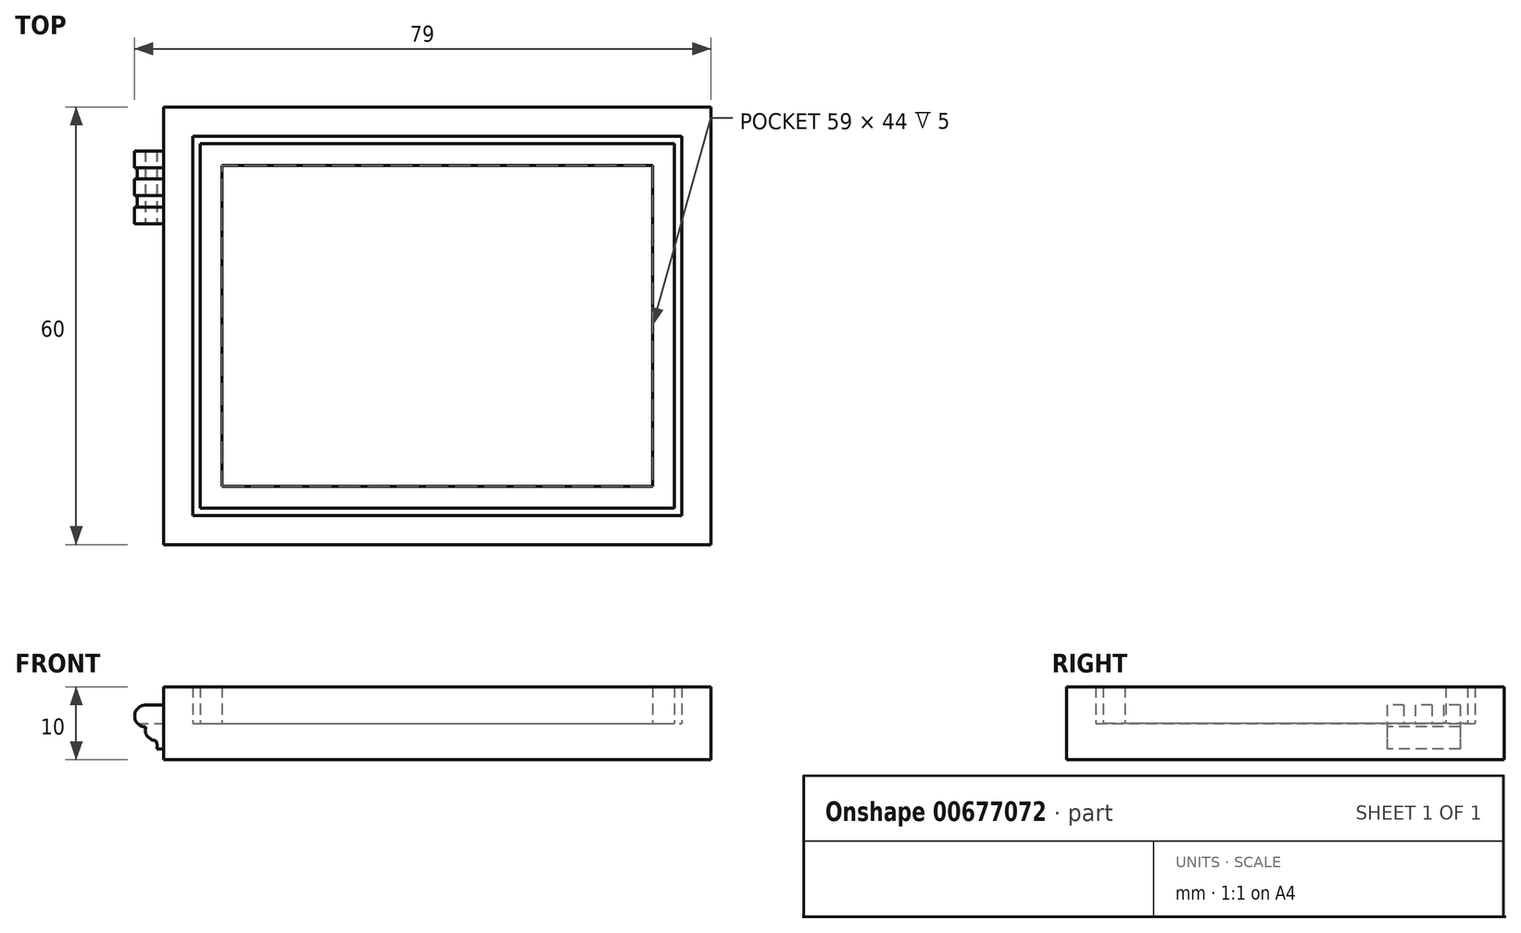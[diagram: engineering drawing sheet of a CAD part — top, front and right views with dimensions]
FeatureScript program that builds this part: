
annotation { "Feature Type Name" : "Feature", "Feature Type Description" : "" }
export const myFeature = defineFeature(function(context is Context, id is Id, definition is map)
    precondition{}
    {
        {
            var Q0;
            Q0=qCreatedBy(makeId("Top.planeOp"),FACE);
            var sketch = newSketch(context, id + "F0", { "sketchPlane" : qUnion([Q0])});
            skLineSegment(sketch, "E0.bottom", {"start": v(-37.5, 30) * mm, "end": v(37.5, 30) * mm});
            skLineSegment(sketch, "E0.top", {"start": v(-37.5, -30) * mm, "end": v(37.5, -30) * mm});
            skLineSegment(sketch, "E0.left", {"start": v(-37.5, 30) * mm, "end": v(-37.5, -30) * mm});
            skLineSegment(sketch, "E0.right", {"start": v(37.5, 30) * mm, "end": v(37.5, -30) * mm});
            skSolve(sketch);
        }
        {
            var Q0;
            Q0 = qSketchRegion(id + "F0", true);
            extrude(context, id + "F1", {"entities" : qUnion([Q0]), "depth" : 5 * mm, "offsetDistance" : 25 * mm});
        }
        {
            var Q0;
            Q0=makeQuery(id+"F1.opExtrude","CAP_FACE",FACE,{"disambiguationData":[OSD([sQuery(id+"F0.wireOp",EDGE,"E0.bottom"),sQuery(id+"F0.wireOp",EDGE,"E0.top"),sQuery(id+"F0.wireOp",EDGE,"E0.left"),sQuery(id+"F0.wireOp",EDGE,"E0.right")])],"isStart":false});
            var sketch = newSketch(context, id + "F2", { "sketchPlane" : qUnion([Q0])});
            skLineSegment(sketch, "E1.bottom", {"start": v(-32.5, 25) * mm, "end": v(32.5, 25) * mm});
            skLineSegment(sketch, "E1.top", {"start": v(-32.5, -25) * mm, "end": v(32.5, -25) * mm});
            skLineSegment(sketch, "E1.left", {"start": v(-32.5, 25) * mm, "end": v(-32.5, -25) * mm});
            skLineSegment(sketch, "E1.right", {"start": v(32.5, 25) * mm, "end": v(32.5, -25) * mm});
            skLineSegment(sketch, "E2.0", {"start": v(-29.5, 22) * mm, "end": v(29.5, 22) * mm});
            skLineSegment(sketch, "E2.1", {"start": v(-29.5, 22) * mm, "end": v(-29.5, -22) * mm});
            skLineSegment(sketch, "E2.2", {"start": v(-29.5, -22) * mm, "end": v(29.5, -22) * mm});
            skLineSegment(sketch, "E2.3", {"start": v(29.5, 22) * mm, "end": v(29.5, -22) * mm});
            skSolve(sketch);
        }
        {
            var Q0;
            Q0 = qSketchRegion(id + "F2", true);
            extrude(context, id + "F3", {"entities" : qUnion([Q0]), "operationType" : NewBodyOperationType.ADD, "depth" : 5 * mm, "offsetDistance" : 25 * mm});
        }
        {
            var Q0;
            {var subQ0=sQuery(id+"F0.wireOp",EDGE,"E0.left");var subQ1=sQuery(id+"F0.wireOp",EDGE,"E0.top");var subQ2=sQuery(id+"F0.wireOp",EDGE,"E0.right");var subQ3=sQuery(id+"F0.wireOp",EDGE,"E0.bottom");Q0=makeQuery(id+"F3.boolean.opBoolean","SPLIT",FACE,{"disambiguationData":[TD([makeQuery(id+"F1.opExtrude","SWEPT_FACE",FACE,{"disambiguationData":[OSD([subQ3])]})])],"derivedFrom":makeQuery(id+"F1.opExtrude","CAP_FACE",FACE,{"disambiguationData":[OSD([subQ3,subQ1,subQ0,subQ2])],"isStart":false})});}
            var sketch = newSketch(context, id + "F4", { "sketchPlane" : qUnion([Q0])});
            skLineSegment(sketch, "E3.bottom", {"start": v(-33.5, -26) * mm, "end": v(33.5, -26) * mm});
            skLineSegment(sketch, "E3.top", {"start": v(-33.5, 26) * mm, "end": v(33.5, 26) * mm});
            skLineSegment(sketch, "E3.left", {"start": v(-33.5, -26) * mm, "end": v(-33.5, 26) * mm});
            skLineSegment(sketch, "E3.right", {"start": v(33.5, -26) * mm, "end": v(33.5, 26) * mm});
            skLineSegment(sketch, "E4.0", {"start": v(-37.5, 30) * mm, "end": v(37.5, 30) * mm});
            skLineSegment(sketch, "E4.1", {"start": v(-37.5, -30) * mm, "end": v(-37.5, 30) * mm});
            skLineSegment(sketch, "E4.2", {"start": v(-37.5, -30) * mm, "end": v(37.5, -30) * mm});
            skLineSegment(sketch, "E4.3", {"start": v(37.5, -30) * mm, "end": v(37.5, 30) * mm});
            skSolve(sketch);
        }
        {
            var Q0;
            Q0 = qSketchRegion(id + "F4", true);
            extrude(context, id + "F5", {"entities" : qUnion([Q0]), "depth" : 5 * mm, "offsetDistance" : 25 * mm});
        }
        {
            var Q0;
            Q0=makeQuery(id+"F1.opExtrude","SWEPT_FACE",FACE,{"disambiguationData":[OSD([sQuery(id+"F0.wireOp",EDGE,"E0.left")])]});
            var sketch = newSketch(context, id + "F6", { "sketchPlane" : qUnion([Q0])});
            skLineSegment(sketch, "E5.bottom", {"start": v(-23.97, 7.5) * mm, "end": v(-21.7, 7.5) * mm});
            skLineSegment(sketch, "E5.top", {"start": v(-23.97, 1.5) * mm, "end": v(-13.97, 1.5) * mm});
            skLineSegment(sketch, "E5.left", {"start": v(-23.97, 7.5) * mm, "end": v(-23.97, 1.5) * mm});
            skLineSegment(sketch, "E5.right", {"start": v(-13.97, 7.5) * mm, "end": v(-13.97, 1.5) * mm});
            skLineSegment(sketch, "E6.top", {"start": v(-21.7, 5) * mm, "end": v(-20.11, 5) * mm});
            skLineSegment(sketch, "E6.left", {"start": v(-21.7, 7.5) * mm, "end": v(-21.7, 5) * mm});
            skLineSegment(sketch, "E6.right", {"start": v(-20.11, 7.5) * mm, "end": v(-20.11, 5) * mm});
            skLineSegment(sketch, "E7.top", {"start": v(-17.83, 5) * mm, "end": v(-16.25, 5) * mm});
            skLineSegment(sketch, "E7.left", {"start": v(-17.83, 7.5) * mm, "end": v(-17.83, 5) * mm});
            skLineSegment(sketch, "E7.right", {"start": v(-16.25, 7.5) * mm, "end": v(-16.25, 5) * mm});
            skLineSegment(sketch, "E8.trimOffspring", {"start": v(-16.25, 7.5) * mm, "end": v(-13.97, 7.5) * mm});
            skLineSegment(sketch, "E9.trimOffspring", {"start": v(-20.11, 7.5) * mm, "end": v(-17.83, 7.5) * mm});
            skSolve(sketch);
        }
        {
            var Q0;
            Q0 = qSketchRegion(id + "F6", true);
            extrude(context, id + "F7", {"entities" : qUnion([Q0]), "operationType" : NewBodyOperationType.ADD, "depth" : 5 * mm, "offsetDistance" : 25 * mm});
        }
        {
            var Q0;
            Q0=makeQuery(id+"F7.opExtrude","SWEPT_FACE",FACE,{"disambiguationData":[OSD([sQuery(id+"F6.wireOp",EDGE,"E5.right")])]});
            var sketch = newSketch(context, id + "F8", { "sketchPlane" : qUnion([Q0])});
            skLineSegment(sketch, "E10.2", {"start": v(-42.5, 1.5) * mm, "end": v(-38.45, 1.5) * mm});
            skArc(sketch, "E11", {"start": v(-40, 7.5) * mm, "mid": v(-41.5, 6) * mm, "end": v(-40, 4.5) * mm});
            skPoint(sketch, "E11.centerSnap0", {"position": v(-40, 7.5) * mm});
            skFitSpline(sketch, "E12", {"points": [v(-40, 4.5) * mm, v(-40, 3.67) * mm, v(-39.7, 3.2) * mm, v(-39.37, 2.9) * mm, v(-39.04, 2.72) * mm, v(-38.75, 2.6) * mm, v(-38.53, 2.46) * mm, v(-38.45, 2.17) * mm, v(-38.42, 1.9) * mm, v(-38.45, 1.5) * mm], "startDerivative": vector(-0.63, -5.59) * mm, "endDerivative": vector(-0.55, -3.92) * mm});
            skPoint(sketch, "E10.1.start.orphan", {"position": v(-42.5, 7.5) * mm});
            skLineSegment(sketch, "E13.0", {"start": v(-42.5, 7.5) * mm, "end": v(-37.5, 7.5) * mm});
            skLineSegment(sketch, "E14.0", {"start": v(-42.5, 7.5) * mm, "end": v(-42.5, 1.5) * mm});
            skPoint(sketch, "E15.orphan", {"position": v(-37.5, 1.5) * mm});
            skSolve(sketch);
        }
        {
            var Q0;
            Q0 = qSketchRegion(id + "F8", true);
            extrude(context, id + "F9", {"entities" : qUnion([Q0]), "operationType" : NewBodyOperationType.REMOVE, "endBound" : BoundingType.THROUGH_ALL, "oppositeDirection" : true, "depth" : 25 * mm, "offsetDistance" : 25 * mm});
        }
    });
